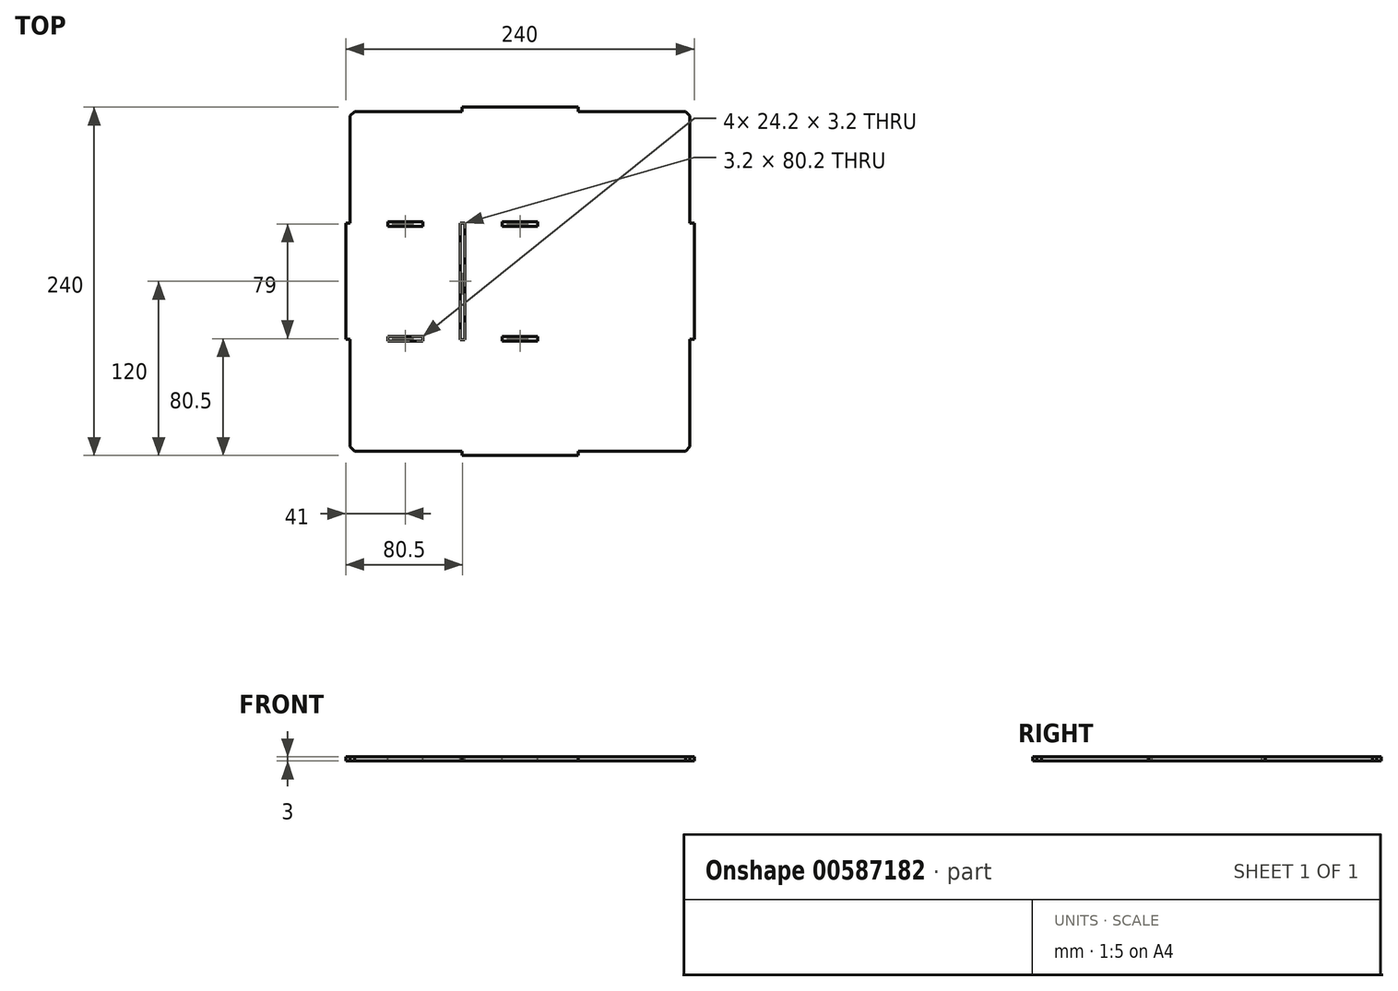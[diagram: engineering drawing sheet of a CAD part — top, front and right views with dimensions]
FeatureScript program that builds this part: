
annotation { "Feature Type Name" : "Feature", "Feature Type Description" : "" }
export const myFeature = defineFeature(function(context is Context, id is Id, definition is map)
    precondition{}
    {
        {
            var Q0;
            Q0=qCreatedBy(makeId("Top.planeOp"),FACE);
            var sketch = newSketch(context, id + "F0", { "sketchPlane" : qUnion([Q0])});
            skLineSegment(sketch, "E0.bottom", {"start": v(117, 117) * mm, "end": v(40, 117) * mm});
            skLineSegment(sketch, "E0.top", {"start": v(117, -117) * mm, "end": v(40, -117) * mm});
            skLineSegment(sketch, "E0.left", {"start": v(117, 117) * mm, "end": v(117, 40) * mm});
            skLineSegment(sketch, "E0.right", {"start": v(-117, 117) * mm, "end": v(-117, 40) * mm});
            skPoint(sketch, "E0.middle", {"position": v(0, 0) * mm});
            skLineSegment(sketch, "E1.top", {"start": v(40, 120) * mm, "end": v(-40, 120) * mm});
            skLineSegment(sketch, "E1.left", {"start": v(40, 117) * mm, "end": v(40, 120) * mm});
            skLineSegment(sketch, "E1.right", {"start": v(-40, 117) * mm, "end": v(-40, 120) * mm});
            skPoint(sketch, "E1.middle", {"position": v(0, 99.54) * mm});
            skLineSegment(sketch, "E2.bottom", {"start": v(-117, -40) * mm, "end": v(-120, -40) * mm});
            skLineSegment(sketch, "E2.top", {"start": v(-117, 40) * mm, "end": v(-120, 40) * mm});
            skLineSegment(sketch, "E2.right", {"start": v(-120, -40) * mm, "end": v(-120, 40) * mm});
            skPoint(sketch, "E2.middle", {"position": v(-88.03, 0) * mm});
            skLineSegment(sketch, "E3.MirrorCS", {"start": v(-40, -117) * mm, "end": v(-40, -120) * mm});
            skLineSegment(sketch, "E4.MirrorCS", {"start": v(40, -120) * mm, "end": v(-40, -120) * mm});
            skLineSegment(sketch, "E5.MirrorCS", {"start": v(40, -117) * mm, "end": v(40, -120) * mm});
            skLineSegment(sketch, "E6.MirrorCS", {"start": v(117, 40) * mm, "end": v(120, 40) * mm});
            skLineSegment(sketch, "E7.MirrorCS", {"start": v(117, -40) * mm, "end": v(120, -40) * mm});
            skLineSegment(sketch, "E8.MirrorCS", {"start": v(120, -40) * mm, "end": v(120, 40) * mm});
            skPoint(sketch, "E9.orphan", {"position": v(-56.07, 40) * mm});
            skLineSegment(sketch, "E10.trimOffspring", {"start": v(-117, -40) * mm, "end": v(-117, -117) * mm});
            skPoint(sketch, "E11.orphan", {"position": v(-56.07, -40) * mm});
            skLineSegment(sketch, "E12.trimOffspring", {"start": v(-40, 117) * mm, "end": v(-117, 117) * mm});
            skPoint(sketch, "E13.orphan", {"position": v(40, 79.08) * mm});
            skPoint(sketch, "E14.orphan", {"position": v(-40, 79.08) * mm});
            skLineSegment(sketch, "E15.trimOffspring", {"start": v(-40, -117) * mm, "end": v(-117, -117) * mm});
            skPoint(sketch, "E16.orphan", {"position": v(-40, -79.08) * mm});
            skPoint(sketch, "E17.orphan", {"position": v(40, -79.08) * mm});
            skPoint(sketch, "E18.orphan", {"position": v(56.07, -40) * mm});
            skLineSegment(sketch, "E19.trimOffspring", {"start": v(117, -40) * mm, "end": v(117, -117) * mm});
            skPoint(sketch, "E20.orphan", {"position": v(56.07, 40) * mm});
            skSolve(sketch);
        }
        {
            var Q0;
            Q0 = qSketchRegion(id + "F0", true);
            extrude(context, id + "F1", {"entities" : qUnion([Q0]), "depth" : 3 * mm, "offsetDistance" : 25 * mm});
        }
        {
            var Q0;
            Q0=makeQuery(id+"F1.opExtrude","SWEPT_EDGE",EDGE,{"disambiguationData":[OSD([sQuery(id+"F0.wireOp",EDGE,"E0.top"),sQuery(id+"F0.wireOp",EDGE,"E19.trimOffspring")])]});
            var Q1;
            Q1=makeQuery(id+"F1.opExtrude","SWEPT_EDGE",EDGE,{"disambiguationData":[OSD([sQuery(id+"F0.wireOp",EDGE,"E0.right"),sQuery(id+"F0.wireOp",EDGE,"E12.trimOffspring")])]});
            var Q2;
            Q2=makeQuery(id+"F1.opExtrude","SWEPT_EDGE",EDGE,{"disambiguationData":[OSD([sQuery(id+"F0.wireOp",EDGE,"E0.bottom"),sQuery(id+"F0.wireOp",EDGE,"E0.left")])]});
            var Q3;
            Q3=makeQuery(id+"F1.opExtrude","SWEPT_EDGE",EDGE,{"disambiguationData":[OSD([sQuery(id+"F0.wireOp",EDGE,"E10.trimOffspring"),sQuery(id+"F0.wireOp",EDGE,"E15.trimOffspring")])]});
            chamfer(context, id + "F2", {"entities" : qUnion([Q0, Q1, Q2, Q3]), "width" : 3 * mm, "tangentPropagation" : true});
        }
        {
            var Q0;
            Q0=makeQuery(id+"F1.opExtrude","CAP_FACE",FACE,{"disambiguationData":[OSD([sQuery(id+"F0.wireOp",EDGE,"E0.bottom"),sQuery(id+"F0.wireOp",EDGE,"E0.top"),sQuery(id+"F0.wireOp",EDGE,"E0.left"),sQuery(id+"F0.wireOp",EDGE,"E0.right"),sQuery(id+"F0.wireOp",EDGE,"E1.top"),sQuery(id+"F0.wireOp",EDGE,"E1.left"),sQuery(id+"F0.wireOp",EDGE,"E1.right"),sQuery(id+"F0.wireOp",EDGE,"E2.bottom"),sQuery(id+"F0.wireOp",EDGE,"E2.top"),sQuery(id+"F0.wireOp",EDGE,"E2.right"),sQuery(id+"F0.wireOp",EDGE,"E3.MirrorCS"),sQuery(id+"F0.wireOp",EDGE,"E4.MirrorCS"),sQuery(id+"F0.wireOp",EDGE,"E5.MirrorCS"),sQuery(id+"F0.wireOp",EDGE,"E6.MirrorCS"),sQuery(id+"F0.wireOp",EDGE,"E7.MirrorCS"),sQuery(id+"F0.wireOp",EDGE,"E8.MirrorCS"),sQuery(id+"F0.wireOp",EDGE,"E10.trimOffspring"),sQuery(id+"F0.wireOp",EDGE,"E12.trimOffspring"),sQuery(id+"F0.wireOp",EDGE,"E15.trimOffspring"),sQuery(id+"F0.wireOp",EDGE,"E19.trimOffspring")])],"isStart":false});
            var sketch = newSketch(context, id + "F3", { "sketchPlane" : qUnion([Q0])});
            skLineSegment(sketch, "E21.bottom", {"start": v(-37.9, 40.1) * mm, "end": v(-41.1, 40.1) * mm});
            skLineSegment(sketch, "E21.top", {"start": v(-37.9, -40.1) * mm, "end": v(-41.1, -40.1) * mm});
            skLineSegment(sketch, "E21.left", {"start": v(-37.9, 40.1) * mm, "end": v(-37.9, -40.1) * mm});
            skLineSegment(sketch, "E21.right", {"start": v(-41.1, 40.1) * mm, "end": v(-41.1, -40.1) * mm});
            skPoint(sketch, "E21.middle", {"position": v(-39.5, 0) * mm});
            skSolve(sketch);
        }
        {
            var Q0;
            Q0 = qSketchRegion(id + "F3", true);
            extrude(context, id + "F4", {"entities" : qUnion([Q0]), "operationType" : NewBodyOperationType.REMOVE, "endBound" : BoundingType.THROUGH_ALL, "oppositeDirection" : true, "depth" : 25 * mm, "offsetDistance" : 25 * mm});
        }
        {
            var Q0;
            Q0=makeQuery(id+"F1.opExtrude","CAP_FACE",FACE,{"disambiguationData":[OSD([sQuery(id+"F0.wireOp",EDGE,"E0.bottom"),sQuery(id+"F0.wireOp",EDGE,"E0.top"),sQuery(id+"F0.wireOp",EDGE,"E0.left"),sQuery(id+"F0.wireOp",EDGE,"E0.right"),sQuery(id+"F0.wireOp",EDGE,"E1.top"),sQuery(id+"F0.wireOp",EDGE,"E1.left"),sQuery(id+"F0.wireOp",EDGE,"E1.right"),sQuery(id+"F0.wireOp",EDGE,"E2.bottom"),sQuery(id+"F0.wireOp",EDGE,"E2.top"),sQuery(id+"F0.wireOp",EDGE,"E2.right"),sQuery(id+"F0.wireOp",EDGE,"E3.MirrorCS"),sQuery(id+"F0.wireOp",EDGE,"E4.MirrorCS"),sQuery(id+"F0.wireOp",EDGE,"E5.MirrorCS"),sQuery(id+"F0.wireOp",EDGE,"E6.MirrorCS"),sQuery(id+"F0.wireOp",EDGE,"E7.MirrorCS"),sQuery(id+"F0.wireOp",EDGE,"E8.MirrorCS"),sQuery(id+"F0.wireOp",EDGE,"E10.trimOffspring"),sQuery(id+"F0.wireOp",EDGE,"E12.trimOffspring"),sQuery(id+"F0.wireOp",EDGE,"E15.trimOffspring"),sQuery(id+"F0.wireOp",EDGE,"E19.trimOffspring")])],"isStart":false});
            var sketch = newSketch(context, id + "F5", { "sketchPlane" : qUnion([Q0])});
            skLineSegment(sketch, "E22.bottom", {"start": v(-66.9, 41.1) * mm, "end": v(-91.1, 41.1) * mm});
            skLineSegment(sketch, "E22.top", {"start": v(-66.9, 37.9) * mm, "end": v(-91.1, 37.9) * mm});
            skLineSegment(sketch, "E22.left", {"start": v(-66.9, 41.1) * mm, "end": v(-66.9, 37.9) * mm});
            skLineSegment(sketch, "E22.right", {"start": v(-91.1, 41.1) * mm, "end": v(-91.1, 37.9) * mm});
            skPoint(sketch, "E22.middle", {"position": v(-79, 39.5) * mm});
            skLineSegment(sketch, "E23.MirrorCS", {"start": v(-66.9, -41.1) * mm, "end": v(-91.1, -41.1) * mm});
            skLineSegment(sketch, "E24.MirrorCS", {"start": v(-66.9, -41.1) * mm, "end": v(-66.9, -37.9) * mm});
            skLineSegment(sketch, "E25.MirrorCS", {"start": v(-66.9, -37.9) * mm, "end": v(-91.1, -37.9) * mm});
            skLineSegment(sketch, "E26.MirrorCS", {"start": v(-91.1, -41.1) * mm, "end": v(-91.1, -37.9) * mm});
            skSolve(sketch);
        }
        {
            var Q0;
            Q0 = qSketchRegion(id + "F5", true);
            extrude(context, id + "F6", {"entities" : qUnion([Q0]), "operationType" : NewBodyOperationType.REMOVE, "endBound" : BoundingType.THROUGH_ALL, "oppositeDirection" : true, "depth" : 25 * mm, "offsetDistance" : 25 * mm});
        }
        {
            var Q0;
            Q0=makeQuery(id+"F1.opExtrude","CAP_FACE",FACE,{"disambiguationData":[OSD([sQuery(id+"F0.wireOp",EDGE,"E0.bottom"),sQuery(id+"F0.wireOp",EDGE,"E0.top"),sQuery(id+"F0.wireOp",EDGE,"E0.left"),sQuery(id+"F0.wireOp",EDGE,"E0.right"),sQuery(id+"F0.wireOp",EDGE,"E1.top"),sQuery(id+"F0.wireOp",EDGE,"E1.left"),sQuery(id+"F0.wireOp",EDGE,"E1.right"),sQuery(id+"F0.wireOp",EDGE,"E2.bottom"),sQuery(id+"F0.wireOp",EDGE,"E2.top"),sQuery(id+"F0.wireOp",EDGE,"E2.right"),sQuery(id+"F0.wireOp",EDGE,"E3.MirrorCS"),sQuery(id+"F0.wireOp",EDGE,"E4.MirrorCS"),sQuery(id+"F0.wireOp",EDGE,"E5.MirrorCS"),sQuery(id+"F0.wireOp",EDGE,"E6.MirrorCS"),sQuery(id+"F0.wireOp",EDGE,"E7.MirrorCS"),sQuery(id+"F0.wireOp",EDGE,"E8.MirrorCS"),sQuery(id+"F0.wireOp",EDGE,"E10.trimOffspring"),sQuery(id+"F0.wireOp",EDGE,"E12.trimOffspring"),sQuery(id+"F0.wireOp",EDGE,"E15.trimOffspring"),sQuery(id+"F0.wireOp",EDGE,"E19.trimOffspring")])],"isStart":false});
            var sketch = newSketch(context, id + "F7", { "sketchPlane" : qUnion([Q0])});
            skLineSegment(sketch, "E27.bottom", {"start": v(12.1, 37.9) * mm, "end": v(-12.1, 37.9) * mm});
            skLineSegment(sketch, "E27.top", {"start": v(12.1, 41.1) * mm, "end": v(-12.1, 41.1) * mm});
            skLineSegment(sketch, "E27.left", {"start": v(12.1, 37.9) * mm, "end": v(12.1, 41.1) * mm});
            skLineSegment(sketch, "E27.right", {"start": v(-12.1, 37.9) * mm, "end": v(-12.1, 41.1) * mm});
            skPoint(sketch, "E27.middle", {"position": v(0, 39.5) * mm});
            skLineSegment(sketch, "E28.bottom", {"start": v(12.1, -37.9) * mm, "end": v(-12.1, -37.9) * mm});
            skLineSegment(sketch, "E28.top", {"start": v(12.1, -41.1) * mm, "end": v(-12.1, -41.1) * mm});
            skLineSegment(sketch, "E28.left", {"start": v(12.1, -37.9) * mm, "end": v(12.1, -41.1) * mm});
            skLineSegment(sketch, "E28.right", {"start": v(-12.1, -37.9) * mm, "end": v(-12.1, -41.1) * mm});
            skPoint(sketch, "E28.middle", {"position": v(0, -39.5) * mm});
            skSolve(sketch);
        }
        {
            var Q0;
            Q0 = qSketchRegion(id + "F7", true);
            extrude(context, id + "F8", {"entities" : qUnion([Q0]), "operationType" : NewBodyOperationType.REMOVE, "endBound" : BoundingType.THROUGH_ALL, "oppositeDirection" : true, "depth" : 25 * mm, "offsetDistance" : 25 * mm});
        }
    });
